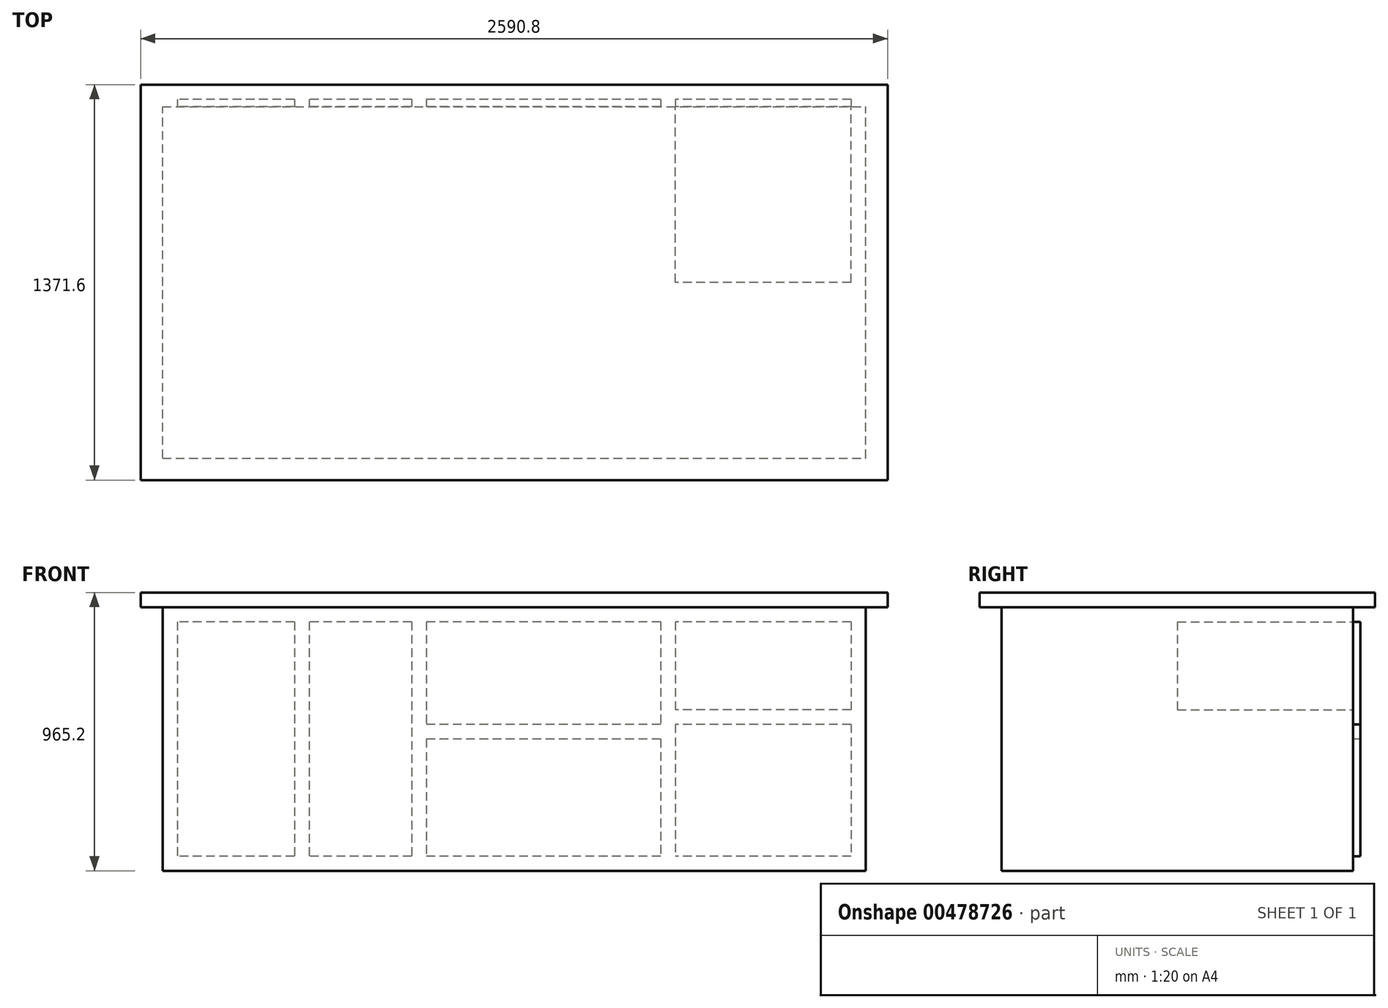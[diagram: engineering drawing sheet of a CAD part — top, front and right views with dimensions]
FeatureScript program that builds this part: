
annotation { "Feature Type Name" : "Feature", "Feature Type Description" : "" }
export const myFeature = defineFeature(function(context is Context, id is Id, definition is map)
    precondition{}
    {
        {
            var Q0;
            Q0=qCreatedBy(makeId("Top.planeOp"),FACE);
            var sketch = newSketch(context, id + "F0", { "sketchPlane" : qUnion([Q0])});
            skLineSegment(sketch, "E0.bottom", {"start": v(-1504.7, -597.54) * mm, "end": v(933.7, -597.54) * mm});
            skLineSegment(sketch, "E0.top", {"start": v(-1504.7, 621.66) * mm, "end": v(933.7, 621.66) * mm});
            skLineSegment(sketch, "E0.left", {"start": v(-1504.7, -597.54) * mm, "end": v(-1504.7, 621.66) * mm});
            skLineSegment(sketch, "E0.right", {"start": v(933.7, -597.54) * mm, "end": v(933.7, 621.66) * mm});
            skSolve(sketch);
        }
        {
            var Q0;
            Q0 = qSketchRegion(id + "F0", true);
            extrude(context, id + "F1", {"entities" : qUnion([Q0]), "depth" : 914.4 * mm, "offsetDistance" : 25.4 * mm});
        }
        {
            var Q0;
            Q0=makeQuery(id+"F1.opExtrude","CAP_FACE",FACE,{"disambiguationData":[OSD([sQuery(id+"F0.wireOp",EDGE,"E0.bottom"),sQuery(id+"F0.wireOp",EDGE,"E0.top"),sQuery(id+"F0.wireOp",EDGE,"E0.left"),sQuery(id+"F0.wireOp",EDGE,"E0.right")])],"isStart":false});
            var sketch = newSketch(context, id + "F2", { "sketchPlane" : qUnion([Q0])});
            skLineSegment(sketch, "E1.bottom", {"start": v(-1580.9, 697.86) * mm, "end": v(1009.9, 697.86) * mm});
            skLineSegment(sketch, "E1.top", {"start": v(-1580.9, -673.74) * mm, "end": v(1009.9, -673.74) * mm});
            skLineSegment(sketch, "E1.left", {"start": v(-1580.9, 697.86) * mm, "end": v(-1580.9, -673.74) * mm});
            skLineSegment(sketch, "E1.right", {"start": v(1009.9, 697.86) * mm, "end": v(1009.9, -673.74) * mm});
            skSolve(sketch);
        }
        {
            var Q0;
            Q0 = qSketchRegion(id + "F2", true);
            extrude(context, id + "F3", {"entities" : qUnion([Q0]), "operationType" : NewBodyOperationType.ADD, "depth" : 50.8 * mm, "offsetDistance" : 25.4 * mm});
        }
        {
            var Q0;
            Q0=makeQuery(id+"F1.opExtrude","SWEPT_FACE",FACE,{"disambiguationData":[OSD([sQuery(id+"F0.wireOp",EDGE,"E0.top")])]});
            var sketch = newSketch(context, id + "F4", { "sketchPlane" : qUnion([Q0])});
            skLineSegment(sketch, "E2.bottom", {"start": v(-882.9, 863.6) * mm, "end": v(-273.3, 863.6) * mm});
            skLineSegment(sketch, "E2.top", {"start": v(-882.9, 558.8) * mm, "end": v(-273.3, 558.8) * mm});
            skLineSegment(sketch, "E2.left", {"start": v(-882.9, 863.6) * mm, "end": v(-882.9, 558.8) * mm});
            skLineSegment(sketch, "E2.right", {"start": v(-273.3, 863.6) * mm, "end": v(-273.3, 558.8) * mm});
            skSolve(sketch);
        }
        {
            var Q0;
            Q0 = qSketchRegion(id + "F4", true);
            extrude(context, id + "F5", {"entities" : qUnion([Q0]), "operationType" : NewBodyOperationType.REMOVE, "oppositeDirection" : true, "depth" : 609.6 * mm, "offsetDistance" : 25.4 * mm});
        }
        {
            var Q0;
            Q0=makeQuery(id+"F1.opExtrude","SWEPT_FACE",FACE,{"disambiguationData":[OSD([sQuery(id+"F0.wireOp",EDGE,"E0.top")])]});
            var sketch = newSketch(context, id + "F6", { "sketchPlane" : qUnion([Q0])});
            skLineSegment(sketch, "E3.bottom", {"start": v(-882.9, 508) * mm, "end": v(-273.3, 508) * mm});
            skLineSegment(sketch, "E3.top", {"start": v(-882.9, 50.8) * mm, "end": v(-273.3, 50.8) * mm});
            skLineSegment(sketch, "E3.left", {"start": v(-882.9, 508) * mm, "end": v(-882.9, 50.8) * mm});
            skLineSegment(sketch, "E3.right", {"start": v(-273.3, 508) * mm, "end": v(-273.3, 50.8) * mm});
            skLineSegment(sketch, "E4.bottom", {"start": v(-222.5, 863.6) * mm, "end": v(590.3, 863.6) * mm});
            skLineSegment(sketch, "E4.top", {"start": v(-222.5, 508) * mm, "end": v(590.3, 508) * mm});
            skLineSegment(sketch, "E4.left", {"start": v(-222.5, 863.6) * mm, "end": v(-222.5, 508) * mm});
            skLineSegment(sketch, "E4.right", {"start": v(590.3, 863.6) * mm, "end": v(590.3, 508) * mm});
            skLineSegment(sketch, "E5.bottom", {"start": v(-222.5, 457.2) * mm, "end": v(590.3, 457.2) * mm});
            skLineSegment(sketch, "E5.top", {"start": v(-222.5, 50.8) * mm, "end": v(590.3, 50.8) * mm});
            skLineSegment(sketch, "E5.left", {"start": v(-222.5, 457.2) * mm, "end": v(-222.5, 50.8) * mm});
            skLineSegment(sketch, "E5.right", {"start": v(590.3, 457.2) * mm, "end": v(590.3, 50.8) * mm});
            skLineSegment(sketch, "E6.bottom", {"start": v(641.1, 863.6) * mm, "end": v(996.7, 863.6) * mm});
            skLineSegment(sketch, "E6.top", {"start": v(641.1, 50.8) * mm, "end": v(996.7, 50.8) * mm});
            skLineSegment(sketch, "E6.left", {"start": v(641.1, 863.6) * mm, "end": v(641.1, 50.8) * mm});
            skLineSegment(sketch, "E6.right", {"start": v(996.7, 863.6) * mm, "end": v(996.7, 50.8) * mm});
            skLineSegment(sketch, "E7.bottom", {"start": v(1047.5, 863.6) * mm, "end": v(1453.9, 863.6) * mm});
            skLineSegment(sketch, "E7.top", {"start": v(1047.5, 50.8) * mm, "end": v(1453.9, 50.8) * mm});
            skLineSegment(sketch, "E7.left", {"start": v(1047.5, 863.6) * mm, "end": v(1047.5, 50.8) * mm});
            skLineSegment(sketch, "E7.right", {"start": v(1453.9, 863.6) * mm, "end": v(1453.9, 50.8) * mm});
            skSolve(sketch);
        }
        {
            var Q0;
            Q0 = qSketchRegion(id + "F6", true);
            extrude(context, id + "F7", {"entities" : qUnion([Q0]), "operationType" : NewBodyOperationType.ADD, "depth" : 25.4 * mm, "offsetDistance" : 25.4 * mm});
        }
    });
